# Revit family: Haworth_LC1_SlingChair
name_source: partatom
category: Furniture
revit_build: Autodesk Revit 2018 (Build: 20170223_1515(x64)
units: mm (PartAtom-declared; Revit-internal decimal feet)

## family parameters
Always vertical = No
Cut with Voids When Loaded = No
OmniClass Number = 23.40.20.00
OmniClass Title = General Furniture and Specialties
Room Calculation Point = No
Shared = No
Work Plane-Based = No

## types (1)
- HCCS-LC1Z
    Actual Depth = 2' - 1 1/2"
    Actual Height = 2' - 1 7/8"
    Actual Width = 1' - 10 7/8"
    Assembly Code = E2020200
    Description = Haworth LC1 Sling Chair
    Frame Finish = Haworth _ Metal _ Chrome
    Glide Finish = Haworth _ Paint _ Black
    Manufacturer = Haworth
    Model = HCCS-LC1Z
    Revision Number = 4
    Size = Verify Final Dim. w/ Haworth
    Spring Finish = Haworth _ Metal _ Brushed Aluminum
    URL = http://www.haworth.com
    URL - Product = http://www.haworth.com
    Warranty = http://www.haworth.com

## geometry (parser evidence)
native form markers: Sweep x2
no freeform markers — native parametric forms only
